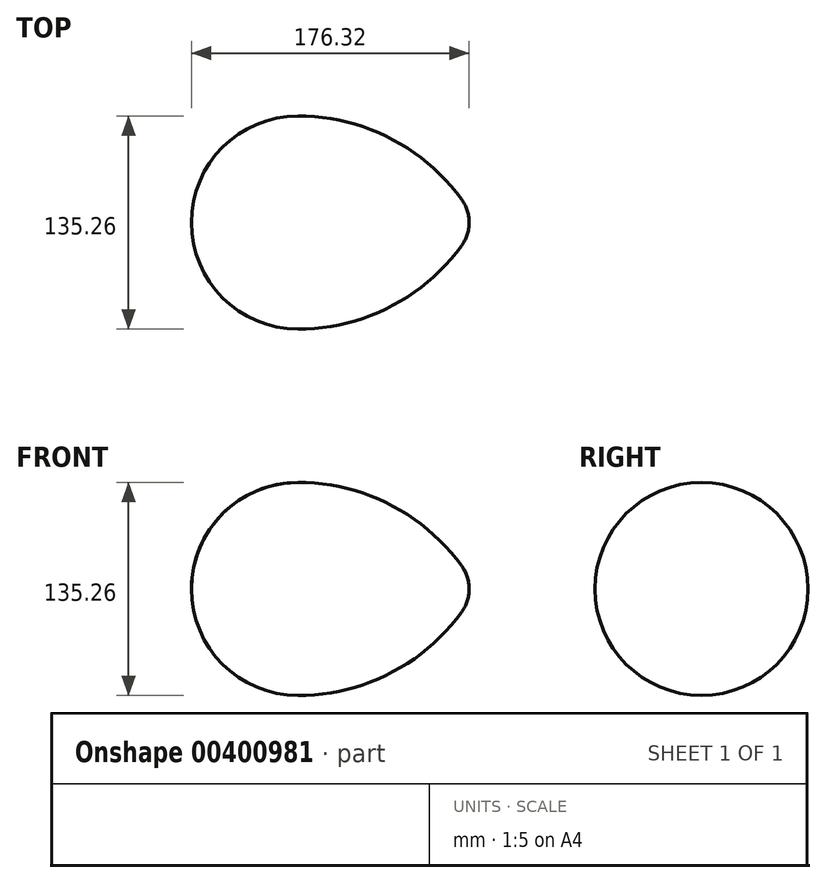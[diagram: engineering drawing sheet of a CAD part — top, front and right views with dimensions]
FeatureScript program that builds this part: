
annotation { "Feature Type Name" : "Feature", "Feature Type Description" : "" }
export const myFeature = defineFeature(function(context is Context, id is Id, definition is map)
    precondition{}
    {
        {
            var Q0;
            Q0=qCreatedBy(makeId("Front.planeOp"),FACE);
            var sketch = newSketch(context, id + "F0", { "sketchPlane" : qUnion([Q0])});
            skLineSegment(sketch, "E0", {"start": v(0, 67.63) * mm, "end": v(0, 42.23) * mm, "construction": true});
            skLineSegment(sketch, "E1", {"start": v(0, -67.63) * mm, "end": v(0, -42.23) * mm, "construction": true});
            skLineSegment(sketch, "E2", {"start": v(0, 42.23) * mm, "end": v(83.3, 0) * mm, "construction": true});
            skLineSegment(sketch, "E3", {"start": v(41.65, 21.12) * mm, "end": v(0, -61.02) * mm, "construction": true});
            skArc(sketch, "E4", {"start": v(103.78, 15.01) * mm, "mid": v(58.18, 53.72) * mm, "end": v(0, 67.63) * mm});
            skLineSegment(sketch, "E5", {"start": v(-67.63, 0) * mm, "end": v(113.26, 0) * mm});
            skPoint(sketch, "E6.orphan", {"position": v(-84.4, 0) * mm});
            skArc(sketch, "E7.trimOffspring", {"start": v(108.7, 0) * mm, "mid": v(107.43, 7.9) * mm, "end": v(103.78, 15.01) * mm});
            skArc(sketch, "E8.trimOffspring", {"start": v(0, 67.63) * mm, "mid": v(-47.82, 47.82) * mm, "end": v(-67.63, 0) * mm});
            skSolve(sketch);
        }
        {
            var Q0;
            Q0 = qSketchRegion(id + "F0", true);
            var Q1;
            Q1=sQuery(id+"F0.wireOp",EDGE,"E5");
            revolve(context, id + "F1", {"entities" : qUnion([Q0]), "axis" : qUnion([Q1]), "revolveType" : RevolveType.FULL});
        }
    });
